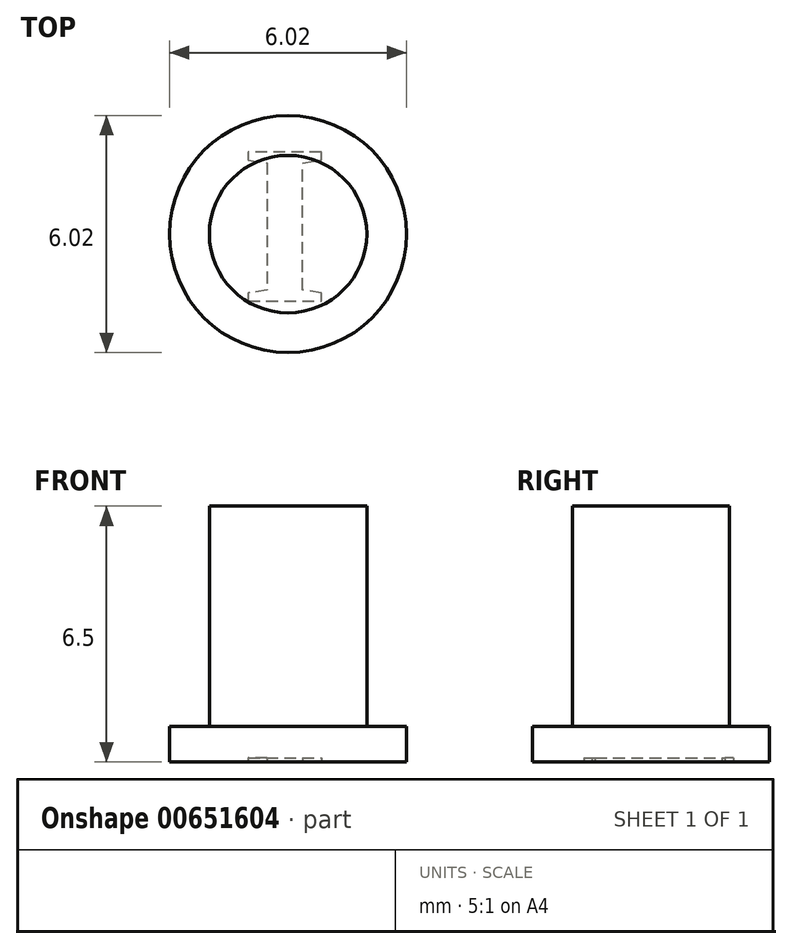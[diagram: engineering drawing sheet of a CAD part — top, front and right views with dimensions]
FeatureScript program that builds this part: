
annotation { "Feature Type Name" : "Feature", "Feature Type Description" : "" }
export const myFeature = defineFeature(function(context is Context, id is Id, definition is map)
    precondition{}
    {
        {
            var Q0;
            Q0=qCreatedBy(makeId("Top.planeOp"),FACE);
            var sketch = newSketch(context, id + "F0", { "sketchPlane" : qUnion([Q0])});
            skCircle(sketch, "E0", {"center": v(0, 0) * mm, "radius": 2 * mm});
            skSolve(sketch);
        }
        {
            var Q0;
            Q0=makeQuery(id+"F0.imprint","IMPRINT",FACE,{"disambiguationData":[TD([[makeQuery(id+"F0.imprint","IMPRINT",EDGE,{"derivedFrom":sQuery(id+"F0.wireOp",EDGE,"E0")}),1.0]])]});
            extrude(context, id + "F1", {"entities" : qUnion([Q0]), "depth" : 5.6 * mm});
        }
        {
            var Q0;
            Q0=makeQuery(id+"F1.opExtrude","CAP_FACE",FACE,{"disambiguationData":[OSD([sQuery(id+"F0.wireOp",EDGE,"E0")])],"isStart":true});
            var sketch = newSketch(context, id + "F2", { "sketchPlane" : qUnion([Q0])});
            skCircle(sketch, "E1", {"center": v(0, 0) * mm, "radius": 3.01 * mm});
            skSolve(sketch);
        }
        {
            var Q0;
            Q0=makeQuery(id+"F2.imprint","IMPRINT",FACE,{"disambiguationData":[TD([[makeQuery(id+"F2.imprint","IMPRINT",EDGE,{"derivedFrom":makeQuery(id+"F1.opExtrude","CAP_EDGE",EDGE,{"disambiguationData":[OSD([sQuery(id+"F0.wireOp",EDGE,"E0")])],"isStart":true})}),-1.0]])]});
            var Q1;
            Q1=makeQuery(id+"F2.imprint","IMPRINT",FACE,{"disambiguationData":[TD([[makeQuery(id+"F2.imprint","IMPRINT",EDGE,{"derivedFrom":sQuery(id+"F2.wireOp",EDGE,"E1")}),1.0]])]});
            extrude(context, id + "F3", {"entities" : qUnion([Q0, Q1]), "operationType" : NewBodyOperationType.ADD, "depth" : .9 * mm});
        }
        {
            var Q0;
            Q0=makeQuery(id+"F3.opExtrude","CAP_FACE",FACE,{"disambiguationData":[OSD([sQuery(id+"F2.wireOp",EDGE,"E1")])],"isStart":false});
            var sketch = newSketch(context, id + "F4", { "sketchPlane" : qUnion([Q0])});
            skText(sketch, "E2", { "text": "I", "fontName": "Tinos-Bold.ttf"});
            const initialGuessF4  = {"E2": [-0.00121, -0.00209, 1, 0, 0.00417]};
            skSetInitialGuess(sketch, initialGuessF4);
            skSolve(sketch);
        }
        {
            var Q0;
            Q0=makeQuery(id+"F4.imprint","IMPRINT",FACE,{"disambiguationData":[TD([[makeQuery(id+"F4.imprint","IMPRINT",EDGE,{"derivedFrom":sQuery(id+"F4.wireOp",EDGE,"E2.sketch_text.stroke-0")}),-1.0]])]});
            extrude(context, id + "F5", {"entities" : qUnion([Q0]), "operationType" : NewBodyOperationType.REMOVE, "oppositeDirection" : true, "depth" : 0.1 * mm});
        }
    });
